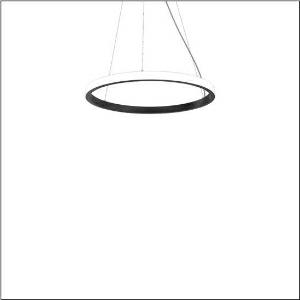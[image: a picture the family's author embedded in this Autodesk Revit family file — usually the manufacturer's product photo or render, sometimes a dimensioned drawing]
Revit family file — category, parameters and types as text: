
# Revit family: silica_21_ring-o_5pjbo2d1104a
name_source: partatom
category: Lighting Fixtures
units: mm (PartAtom-declared; Revit-internal decimal feet)

## family parameters
Cut with Voids When Loaded = No
Host = Face
Light Source = No
Part Type = Normal
Room Calculation Point = No
Round Connector Dimension = Use Diameter
Shared = No

## types (1)
- Silica 21 Ring-O (1 x LED, 4700 lm, 80 W, 3000K)
    Apparent Load = 80 VA
    CIE Flux Codes = 2 16 49 50 100
    Color Rendering = 80
    Color Temperature = 3000K
    Default Elevation = 1800 mm
    Description = Silica 21 Ring-O, suspended luminaire, of PMMA, frosted, light emission: outer ring side luminous distribution, primary light characteristic: symmetric, installation type: suspended mounting, LED, rated luminous flux: 4.700lm, luminous efficacy: 59lm/W, light colour: 830, colour temperature: 3000K, control gear: DALI 2, with terminal, 5-pole, mains connection: 230V, AC/DC, 0/50..60Hz, rated input power: 80W, housing, of extruded aluminium section, jet black (RAL 9005), diameter: 810mm, ceiling canopy, jet black (RAL 9005), protection rating (lamp compartment): IP40, insulation class (complete): insulation class I (protective earthing), certification: CE, impact resistance: IK02, permissible operating ambient temperature: 0..+35°C, packaging unit: 1 piece
    Height = 48 mm  [stored 0.15748 ft]
    Lamp = 1 x LED
    Lamp Light Flux = 4700 lm
    Lamp Power = 80 W
    Lamp count = 1
    Length = 810 mm
    Luminous efficacy = 59 lm/W
    Manufacturer = Siteco
    ModVariant = No
    Model = 5PJBO2D1104A
    Mounting Place = Ceiling
    Mounting Type = Pendant
    Number of Poles = 1
    OnlyDefault = Yes
    Power Factor = 1
    Product Name = Silica 21 Ring-O
    Product group = suspended luminaire
    ProductGroupID = 904
    Protection Class = Protection class I
    Protection Degree = IP 40
    RLX_Detail_Level = 1
    RLX_Emergency_Light_Flux = 0 lm
    RLX_Emergency_Type = 0
    RLX_Emergency_Type_DB = No
    RlxData = <blob elided: 14065 chars, md5=4646836f>
    Socket = socket
    Standby Power = 0 W
    System Light Flux = 4700 lm
    System Power = 80 W
    Type Comments = Product without accessories
    Type Image = l_1258381.jpg
    URL = http://relux.com
    VarID = ---
    Voltage = 0 V
    Weight = 0.00 kg
    Width = 0 mm  [stored 0 ft]

note: [stored X ft] marks values corroborated as IEEE doubles in the binary element streams (Revit-internal decimal feet)

## geometry (parser evidence)
native form markers: Sweep x14
no freeform markers — native parametric forms only
